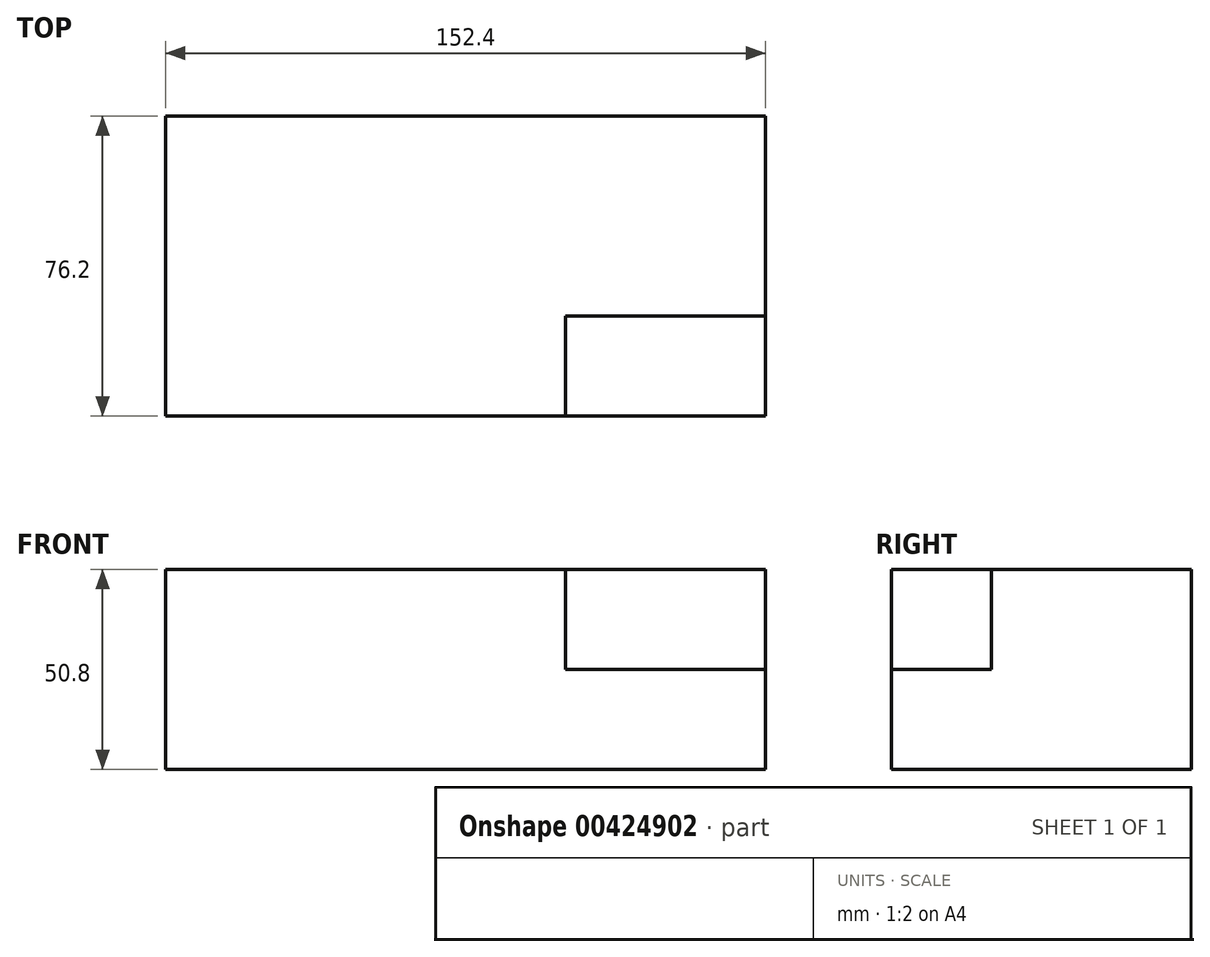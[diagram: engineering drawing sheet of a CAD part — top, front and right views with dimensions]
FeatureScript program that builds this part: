
annotation { "Feature Type Name" : "Feature", "Feature Type Description" : "" }
export const myFeature = defineFeature(function(context is Context, id is Id, definition is map)
    precondition{}
    {
        {
            var Q0;
            Q0=qCreatedBy(makeId("Front.planeOp"),FACE);
            var sketch = newSketch(context, id + "F0", { "sketchPlane" : qUnion([Q0])});
            skLineSegment(sketch, "E0", {"start": v(0, 0) * mm, "end": v(152.4, 0) * mm});
            skLineSegment(sketch, "E1", {"start": v(152.4, 0) * mm, "end": v(152.4, 50.8) * mm});
            skLineSegment(sketch, "E2", {"start": v(152.4, 50.8) * mm, "end": v(0, 50.8) * mm});
            skLineSegment(sketch, "E3", {"start": v(0, 50.8) * mm, "end": v(0, 0) * mm});
            skSolve(sketch);
        }
        {
            var Q0;
            Q0 = qSketchRegion(id + "F0", true);
            extrude(context, id + "F1", {"entities" : qUnion([Q0]), "depth" : 76.2 * mm});
        }
        {
            var Q0;
            Q0=makeQuery(id+"F1.opExtrude","CAP_FACE",FACE,{"disambiguationData":[OSD([sQuery(id+"F0.wireOp",EDGE,"E0"),sQuery(id+"F0.wireOp",EDGE,"E1"),sQuery(id+"F0.wireOp",EDGE,"E2"),sQuery(id+"F0.wireOp",EDGE,"E3")])],"isStart":false});
            var sketch = newSketch(context, id + "F2", { "sketchPlane" : qUnion([Q0])});
            skLineSegment(sketch, "E4", {"start": v(152.4, 50.8) * mm, "end": v(101.6, 50.8) * mm});
            skLineSegment(sketch, "E5", {"start": v(101.6, 50.8) * mm, "end": v(101.6, 25.4) * mm});
            skLineSegment(sketch, "E6", {"start": v(101.6, 25.4) * mm, "end": v(152.4, 25.4) * mm});
            skLineSegment(sketch, "E7", {"start": v(152.4, 50.8) * mm, "end": v(152.4, 25.4) * mm});
            skSolve(sketch);
        }
        {
            var Q0;
            Q0=qCreatedBy(makeId("Top.planeOp"),FACE);
            var sketch = newSketch(context, id + "F3", { "sketchPlane" : qUnion([Q0])});
            skSolve(sketch);
        }
        {
            var Q0;
            Q0 = qSketchRegion(id + "F3", true);
            var Q1;
            Q1=makeQuery(id+"F2.imprint","IMPRINT",FACE,{"disambiguationData":[TD([[makeQuery(id+"F2.imprint","IMPRINT",EDGE,{"derivedFrom":sQuery(id+"F2.wireOp",EDGE,"E4")}),1.0]])]});
            extrude(context, id + "F4", {"entities" : qUnion([Q0, Q1]), "operationType" : NewBodyOperationType.REMOVE, "oppositeDirection" : true, "depth" : 25.4 * mm});
        }
    });
